# Revit family: QF_MACOM_RPTx-AITP
name_source: partatom
category: Equipamento especial
units: mm (PartAtom-declared; Revit-internal decimal feet)

## family parameters
Com base no plano de trabalho = Não
Compartilhado = Não
Corte com vazios quando carregada = Não
Cota do conector redondo = Utilizar diâmetro
Número OmniClass = 23.40.40.11.11.11
Ponto de cálculo do ambiente = Não
Sempre na vertical = Sim
Tipo de parte = Normal
Título OmniClass = Refrigerators

## types (3) — shared parameters
Elevação padrão = 0 mm
Fabricante = MACOM
URL = https://www.acosmacom.com.br
Work Temperature (Cabeçote) = +1ºC a +5ºC
Work Temperature (Gabinete) = +1ºC a +4ºC

## per-type parameters (varying)
| type | Center Handle | Defrost Power | Descrição | Door 3 | Door 4 | GN's Capacity (1/3-150) | Handle Center | Handle Left | Handle Right | Length Actual | Location Separate Door | Number of Doors | Separate Door | Volume |
| RPT4-AITP | 1250,5 mm | 1189 W | REFRIG HORIZ PREP TABLE MACOM, PIZZA P/ 12 GNS 1/3-150, 4 PORTAS INOX, 32 TRILHOS, ALTILENO-2498X800X900 | Sim | Sim | 12 | Não | 561,75 mm | 561,75 mm | 2501 mm | 1250,5 mm | 4 | 600 mm | 2,41 m³ |
| RPT2-AITP | 719,5 mm | 807 W | REFRIG HORIZ PREP TABLE MACOM, PIZZA P/ 7 GNS 1/3-150, 2 PORTAS INOX, 24 TRILHOS, ALTILENO, RODIZIOS 5 - 1435X800X900 | Não | Não | 7 | Sim | 474,15 mm | 384 mm | 1439 mm | 895 mm | 2 | 10 mm | 1,38 m³ |
| RPT3-AITP | 985 mm | 1178 W | REFRIG HORIZ PREP TABLE MACOM, PIZZA P/ 9 GNS 1/3-150, 3 PORTAS INOX, 24 TRILHOS, ALTILENO, RODIZIO Ø5-1967X800X900 | Sim | Não | 9 | Não | 474,15 mm | 384 mm | 1970 mm | 895 mm | 3 | 600 mm | 1,89 m³ |

note: column(s) folded — value = type name in every type: Modelo

## geometry (parser evidence)
native form markers: Sweep x4
no freeform markers — native parametric forms only
